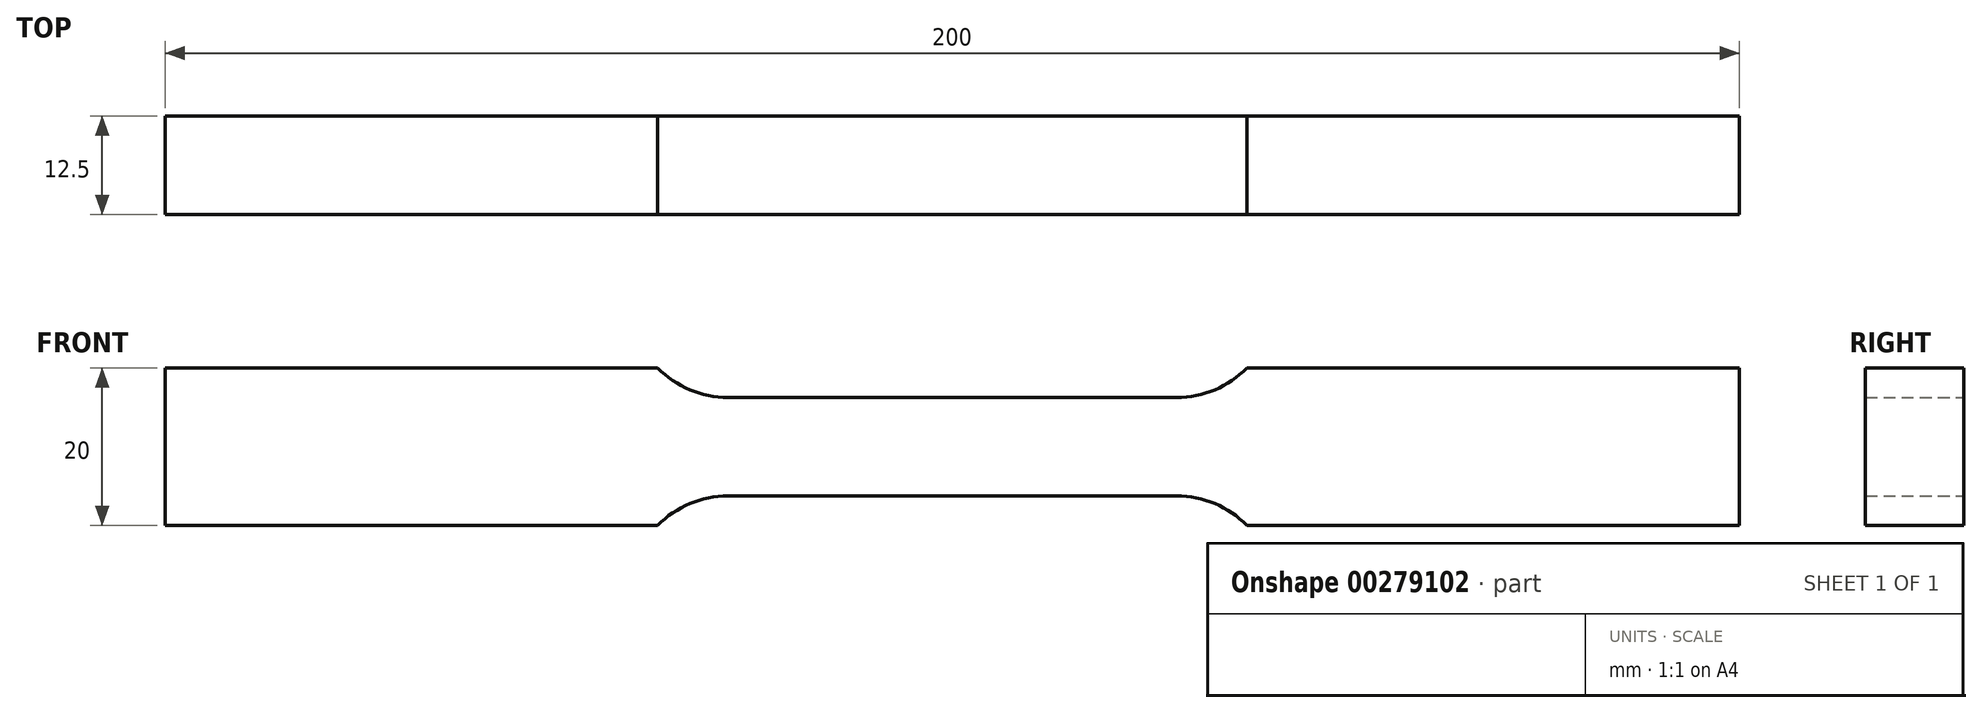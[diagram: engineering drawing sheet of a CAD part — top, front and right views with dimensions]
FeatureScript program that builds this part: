
annotation { "Feature Type Name" : "Feature", "Feature Type Description" : "" }
export const myFeature = defineFeature(function(context is Context, id is Id, definition is map)
    precondition{}
    {
        {
            var Q0;
            Q0=qCreatedBy(makeId("Front.planeOp"),FACE);
            var sketch = newSketch(context, id + "F0", { "sketchPlane" : qUnion([Q0])});
            skLineSegment(sketch, "E0", {"start": v(0, 6.25) * mm, "end": v(28.5, 6.25) * mm});
            skArc(sketch, "E1", {"start": v(28.5, 6.25) * mm, "mid": v(33.34, 7.23) * mm, "end": v(37.43, 10) * mm});
            skLineSegment(sketch, "E2", {"start": v(37.43, 10) * mm, "end": v(100, 10) * mm});
            skLineSegment(sketch, "E3.MirrorCS", {"start": v(37.43, -10) * mm, "end": v(100, -10) * mm});
            skLineSegment(sketch, "E4.MirrorCS", {"start": v(0, -6.25) * mm, "end": v(28.5, -6.25) * mm});
            skArc(sketch, "E5.MirrorCS", {"start": v(28.5, -6.25) * mm, "mid": v(33.34, -7.23) * mm, "end": v(37.43, -10) * mm});
            skArc(sketch, "E6.MirrorCS", {"start": v(-28.5, -6.25) * mm, "mid": v(-33.34, -7.23) * mm, "end": v(-37.43, -10) * mm});
            skLineSegment(sketch, "E7.MirrorCS", {"start": v(0, 6.25) * mm, "end": v(-28.5, 6.25) * mm});
            skArc(sketch, "E8.MirrorCS", {"start": v(-28.5, 6.25) * mm, "mid": v(-33.34, 7.23) * mm, "end": v(-37.43, 10) * mm});
            skLineSegment(sketch, "E9.MirrorCS", {"start": v(-37.43, -10) * mm, "end": v(-100, -10) * mm});
            skLineSegment(sketch, "E10.MirrorCS", {"start": v(0, -6.25) * mm, "end": v(-28.5, -6.25) * mm});
            skLineSegment(sketch, "E11.MirrorCS", {"start": v(-37.43, 10) * mm, "end": v(-100, 10) * mm});
            skLineSegment(sketch, "E12", {"start": v(-100, 10) * mm, "end": v(-100, -10) * mm});
            skLineSegment(sketch, "E13", {"start": v(100, 10) * mm, "end": v(100, -10) * mm});
            skSolve(sketch);
        }
        {
            var Q0;
            Q0=makeQuery(id+"F0.imprint","IMPRINT",FACE,{"disambiguationData":[TD([[makeQuery(id+"F0.imprint","IMPRINT",EDGE,{"derivedFrom":sQuery(id+"F0.wireOp",EDGE,"E0")}),-1.0]])]});
            extrude(context, id + "F1", {"entities" : qUnion([Q0]), "endBound" : BoundingType.SYMMETRIC, "depth" : 12.5 * mm});
        }
    });
